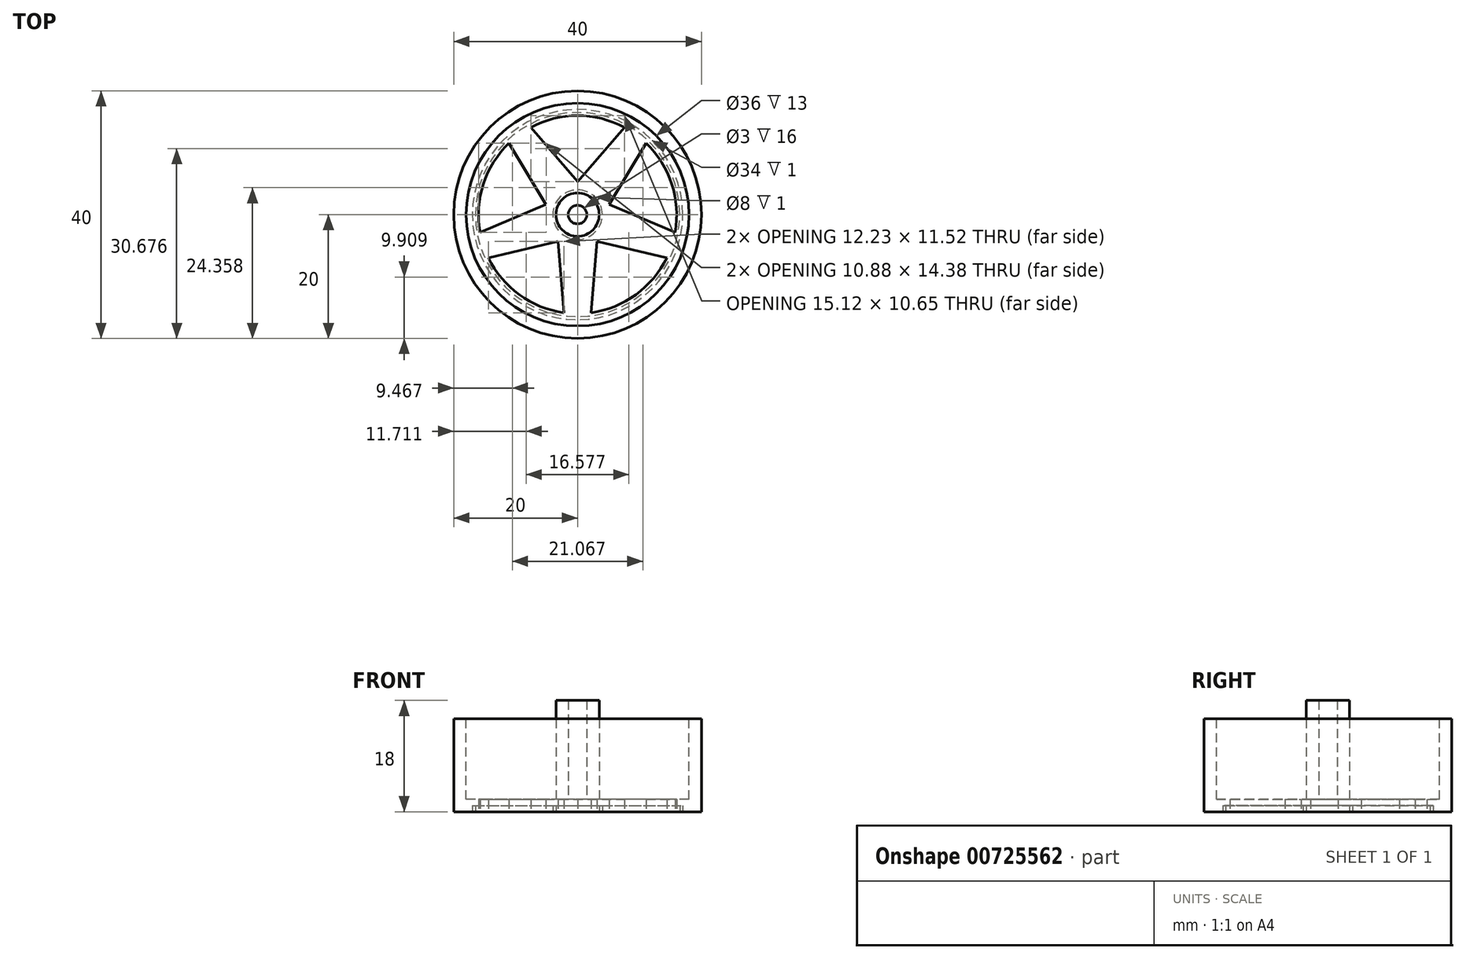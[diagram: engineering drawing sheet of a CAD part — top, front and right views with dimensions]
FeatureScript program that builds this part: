
annotation { "Feature Type Name" : "Feature", "Feature Type Description" : "" }
export const myFeature = defineFeature(function(context is Context, id is Id, definition is map)
    precondition{}
    {
        {
            var Q0;
            Q0=qCreatedBy(makeId("Top.planeOp"),FACE);
            var sketch = newSketch(context, id + "F0", { "sketchPlane" : qUnion([Q0])});
            skCircle(sketch, "E0", {"center": v(0, 0) * mm, "radius": 20 * mm});
            skSolve(sketch);
        }
        {
            var Q0;
            Q0=makeQuery(id+"F0.imprint","IMPRINT",FACE,{"disambiguationData":[TD([[makeQuery(id+"F0.imprint","IMPRINT",EDGE,{"derivedFrom":sQuery(id+"F0.wireOp",EDGE,"E0")}),1.0]])]});
            extrude(context, id + "F1", {"entities" : qUnion([Q0]), "depth" : 15 * mm, "offsetDistance" : 25 * mm});
        }
        {
            var Q0;
            Q0=makeQuery(id+"F1.opExtrude","CAP_FACE",FACE,{"disambiguationData":[OSD([sQuery(id+"F0.wireOp",EDGE,"E0")])],"isStart":false});
            var sketch = newSketch(context, id + "F2", { "sketchPlane" : qUnion([Q0])});
            skCircle(sketch, "E1", {"center": v(0, 0) * mm, "radius": 18 * mm});
            skSolve(sketch);
        }
        {
            var Q0;
            Q0=makeQuery(id+"F2.imprint","IMPRINT",FACE,{"disambiguationData":[TD([[makeQuery(id+"F2.imprint","IMPRINT",EDGE,{"derivedFrom":sQuery(id+"F2.wireOp",EDGE,"E1")}),1.0]])]});
            extrude(context, id + "F3", {"entities" : qUnion([Q0]), "operationType" : NewBodyOperationType.REMOVE, "oppositeDirection" : true, "depth" : 13 * mm, "offsetDistance" : 25 * mm});
        }
        {
            var Q0;
            Q0=makeQuery(id+"F3.boolean.opBoolean","COPY",FACE,{"derivedFrom":makeQuery(id+"F3.opExtrude","CAP_FACE",FACE,{"disambiguationData":[OSD([sQuery(id+"F2.wireOp",EDGE,"E1")])],"isStart":false})});
            var sketch = newSketch(context, id + "F4", { "sketchPlane" : qUnion([Q0])});
            skCircle(sketch, "E2", {"center": v(0, 0) * mm, "radius": 1.5 * mm});
            skCircle(sketch, "E3", {"center": v(0, 0) * mm, "radius": 3.5 * mm});
            skSolve(sketch);
        }
        {
            var Q0;
            Q0=makeQuery(id+"F1.opExtrude","CAP_FACE",FACE,{"disambiguationData":[OSD([sQuery(id+"F0.wireOp",EDGE,"E0")])],"isStart":true});
            var sketch = newSketch(context, id + "F5", { "sketchPlane" : qUnion([Q0])});
            skLineSegment(sketch, "E4", {"start": v(0, 0) * mm, "end": v(2, 0) * mm});
            skLineSegment(sketch, "E5", {"start": v(2.17, 15.85) * mm, "end": v(3.15, 4.33) * mm});
            skLineSegment(sketch, "E6.MirrorCS", {"start": v(-2.17, 15.85) * mm, "end": v(-3.15, 4.33) * mm});
            skLineSegment(sketch, "E7.1.0", {"start": v(-15.75, 2.83) * mm, "end": v(-5.1, -1.65) * mm});
            skLineSegment(sketch, "E7.1.4", {"start": v(-14.4, 6.96) * mm, "end": v(-3.15, 4.33) * mm});
            skLineSegment(sketch, "E7.2.0", {"start": v(-7.56, -14.1) * mm, "end": v(0, -5.35) * mm});
            skLineSegment(sketch, "E7.2.4", {"start": v(-11.07, -11.55) * mm, "end": v(-5.1, -1.65) * mm});
            skLineSegment(sketch, "E7.3.0", {"start": v(11.07, -11.55) * mm, "end": v(5.1, -1.65) * mm});
            skLineSegment(sketch, "E7.3.4", {"start": v(7.56, -14.1) * mm, "end": v(0, -5.35) * mm});
            skLineSegment(sketch, "E7.4.0", {"start": v(14.4, 6.96) * mm, "end": v(3.15, 4.33) * mm});
            skLineSegment(sketch, "E7.4.4", {"start": v(15.75, 2.83) * mm, "end": v(5.1, -1.65) * mm});
            skPoint(sketch, "E7.center", {"position": v(0, 0) * mm});
            skArc(sketch, "E8", {"start": v(-2.17, 15.85) * mm, "mid": v(-9.4, 12.94) * mm, "end": v(-14.4, 6.96) * mm});
            skPoint(sketch, "E9.orphan", {"position": v(-2, 17.89) * mm});
            skPoint(sketch, "E10.trimOffspring.end.orphan", {"position": v(2, 17.89) * mm});
            skPoint(sketch, "E11.orphan", {"position": v(16.4, 7.43) * mm});
            skPoint(sketch, "E12.orphan", {"position": v(17.63, 3.63) * mm});
            skPoint(sketch, "E13.orphan", {"position": v(12.13, -13.3) * mm});
            skPoint(sketch, "E14.orphan", {"position": v(-8.9, -15.65) * mm});
            skPoint(sketch, "E15.orphan", {"position": v(-17.63, 3.63) * mm});
            skPoint(sketch, "E16.orphan", {"position": v(-16.4, 7.43) * mm});
            skCircle(sketch, "E17", {"center": v(0, 0) * mm, "radius": 16.5 * mm});
            skCircle(sketch, "E18", {"center": v(0, 0) * mm, "radius": 17 * mm});
            skArc(sketch, "E19.trimOffspring", {"start": v(14.4, 6.96) * mm, "mid": v(9.4, 12.94) * mm, "end": v(2.17, 15.85) * mm});
            skArc(sketch, "E20.trimOffspring", {"start": v(11.07, -11.55) * mm, "mid": v(15.22, -4.94) * mm, "end": v(15.75, 2.83) * mm});
            skArc(sketch, "E21.trimOffspring", {"start": v(-7.56, -14.1) * mm, "mid": v(0, -16) * mm, "end": v(7.56, -14.1) * mm});
            skArc(sketch, "E22.trimOffspring", {"start": v(-15.75, 2.83) * mm, "mid": v(-15.22, -4.94) * mm, "end": v(-11.07, -11.55) * mm});
            skSolve(sketch);
        }
        {
            var Q0;
            Q0=makeQuery(id+"F4.imprint","IMPRINT",FACE,{"disambiguationData":[TD([[makeQuery(id+"F4.imprint","IMPRINT",EDGE,{"derivedFrom":sQuery(id+"F4.wireOp",EDGE,"E2")}),-1.0]])]});
            extrude(context, id + "F6", {"entities" : qUnion([Q0]), "operationType" : NewBodyOperationType.ADD, "depth" : 16 * mm, "offsetDistance" : 25 * mm});
        }
        {
            var Q0;
            Q0=makeQuery(id+"F5.imprint","IMPRINT",FACE,{"disambiguationData":[TD([[makeQuery(id+"F5.imprint","IMPRINT",EDGE,{"derivedFrom":sQuery(id+"F5.wireOp",EDGE,"E7.2.0")}),-1.0]])]});
            var Q1;
            Q1=makeQuery(id+"F5.imprint","IMPRINT",FACE,{"disambiguationData":[TD([[makeQuery(id+"F5.imprint","IMPRINT",EDGE,{"derivedFrom":sQuery(id+"F5.wireOp",EDGE,"E7.1.0")}),-1.0]])]});
            var Q2;
            Q2=makeQuery(id+"F5.imprint","IMPRINT",FACE,{"disambiguationData":[TD([[makeQuery(id+"F5.imprint","IMPRINT",EDGE,{"derivedFrom":sQuery(id+"F5.wireOp",EDGE,"E6.MirrorCS")}),-1.0]])]});
            var Q3;
            Q3=makeQuery(id+"F5.imprint","IMPRINT",FACE,{"disambiguationData":[TD([[makeQuery(id+"F5.imprint","IMPRINT",EDGE,{"derivedFrom":sQuery(id+"F5.wireOp",EDGE,"E5")}),1.0]])]});
            var Q4;
            Q4=makeQuery(id+"F5.imprint","IMPRINT",FACE,{"disambiguationData":[TD([[makeQuery(id+"F5.imprint","IMPRINT",EDGE,{"derivedFrom":sQuery(id+"F5.wireOp",EDGE,"E7.3.0")}),-1.0]])]});
            var Q5;
            Q5=makeQuery(id+"F6.opExtrude","CAP_FACE",FACE,{"disambiguationData":[OSD([sQuery(id+"F4.wireOp",EDGE,"E2"),sQuery(id+"F4.wireOp",EDGE,"E3")])],"isStart":false});
            extrude(context, id + "F7", {"entities" : qUnion([Q0, Q1, Q2, Q3, Q4, Q5]), "operationType" : NewBodyOperationType.REMOVE, "oppositeDirection" : true, "depth" : 2 * mm, "offsetDistance" : 25 * mm});
        }
        {
            var Q0;
            Q0=qSketchRegion(id+"F5",true);
            extrude(context, id + "F8", {"entities" : qUnion([Q0]), "operationType" : NewBodyOperationType.REMOVE, "oppositeDirection" : true, "depth" : 1 * mm});
        }
        {
            var Q0;
            Q0=makeQuery(id+"F8.boolean.opBoolean","SPLIT",FACE,{"disambiguationData":[TD([makeQuery(id+"F7.boolean.opBoolean","COPY",FACE,{"derivedFrom":makeQuery(id+"F7.opExtrude","SWEPT_FACE",FACE,{"disambiguationData":[OSD([sQuery(id+"F5.wireOp",EDGE,"E5")])]})})])],"derivedFrom":makeQuery(id+"F1.opExtrude","CAP_FACE",FACE,{"disambiguationData":[OSD([sQuery(id+"F0.wireOp",EDGE,"E0")])],"isStart":true})});
            var sketch = newSketch(context, id + "F9", { "sketchPlane" : qUnion([Q0])});
            skCircle(sketch, "E23", {"center": v(0, 0) * mm, "radius": 3.5 * mm});
            skCircle(sketch, "E24", {"center": v(0, 0) * mm, "radius": 4 * mm});
            skSolve(sketch);
        }
        {
            var Q0;
            Q0=makeQuery(id+"F9.imprint","IMPRINT",FACE,{"disambiguationData":[TD([[makeQuery(id+"F9.imprint","IMPRINT",EDGE,{"derivedFrom":sQuery(id+"F9.wireOp",EDGE,"E23")}),-1.0]])]});
            extrude(context, id + "F10", {"entities" : qUnion([Q0]), "operationType" : NewBodyOperationType.REMOVE, "oppositeDirection" : true, "depth" : 1 * mm});
        }
    });
